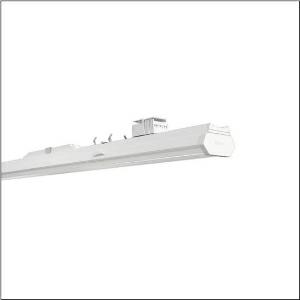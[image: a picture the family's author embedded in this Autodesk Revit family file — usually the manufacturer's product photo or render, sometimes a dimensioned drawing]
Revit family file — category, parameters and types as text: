
# Revit family: licross_r__11_protected_ho_51tp12cn4exm_ba42
name_source: partatom
category: Lighting Fixtures
units: mm (PartAtom-declared; Revit-internal decimal feet)

## family parameters
Cut with Voids When Loaded = No
Host = Face
Light Source = No
Part Type = Normal
Room Calculation Point = No
Round Connector Dimension = Use Diameter
Shared = No

## types (1)
- --- (1 x LED, 14240 lm, 77.6 W, 4000K)
    Apparent Load = 78 VA
    CIE Flux Codes = 70 91 97 98 100
    Color Rendering = 80
    Color Temperature = 4000K
    Default Elevation = 1800 mm
    Description = Licross® 11 Protected HO, luminaire insert, of sheet steel, galvanised, coil coated, white, length: 1.500mm, width: 90mm, height: 101mm, LED rated luminous flux: 14.240lm, light colour: 840, control gear: ON/OFF Multilumen, CLOi, with plug, 3-pole, with phase selection, mains connection: 220..240V, AC, 50/60Hz, halogen-free wiring, primary light control with lens, of plastic, primary optical cover: cover, of PMMA, light emission: direct with ceiling illumination distribution, primary light characteristic: symmetric, protection rating (complete): IP64, insulation class (complete): insulation class I (protective earthing), certification: CE, ENEC, VDE, UKCA, protection symbol: D if used in an environment with conductive dust loads with corresponding accessories, impact resistance: IK06, permissible ambient temperature for indoor applications: -35..+35°C, corresponds to IFS (International Featured Standards) requirements for safety and quality in the food industry, reducing of maximum allowable ambient temperature of 5°C with ceiling mounting, LABS conformity tested according to VDMA 24364:2018-05, packaging unit: 1 piece
    Height = 92 mm
    Lamp = 1 x LED
    Lamp Light Flux = 14240 lm
    Lamp Power = 77.6 W
    Lamp count = 1
    Length = 1500 mm
    Luminous efficacy = 184 lm/W
    Manufacturer = Siteco
    ModVariant = No
    Model = 51TP12CN4EXM
    Mounting Place = Ceiling
    Mounting Type = Pendant
    Number of Poles = 1
    OnlyDefault = Yes
    Power Factor = 1
    Product Name = Licross® 11 Protected HO
    Product group = luminaire insert
    ProductGroupID = 902
    Protection Class = Protection class I
    Protection Degree = IP 64
    RLX_Detail_Level = 1
    RlxData = <blob elided: 22061 chars, md5=88b60a77>
    Socket = socket
    Standby Power = 0 W
    System Light Flux = 14240 lm
    System Power = 78 W
    Type Comments = factory setting: luminous flux: 100 % | (A | C | E) | 181 mA
    Type Image = l_1256148.jpg
    URL = http://relux.com
    VarID = @adj_003887
    Voltage = 0 V
    Weight = 0.00 kg
    Width = 88 mm

## geometry (parser evidence)
native form markers: Blend x4, Sweep x13
no freeform markers — native parametric forms only
